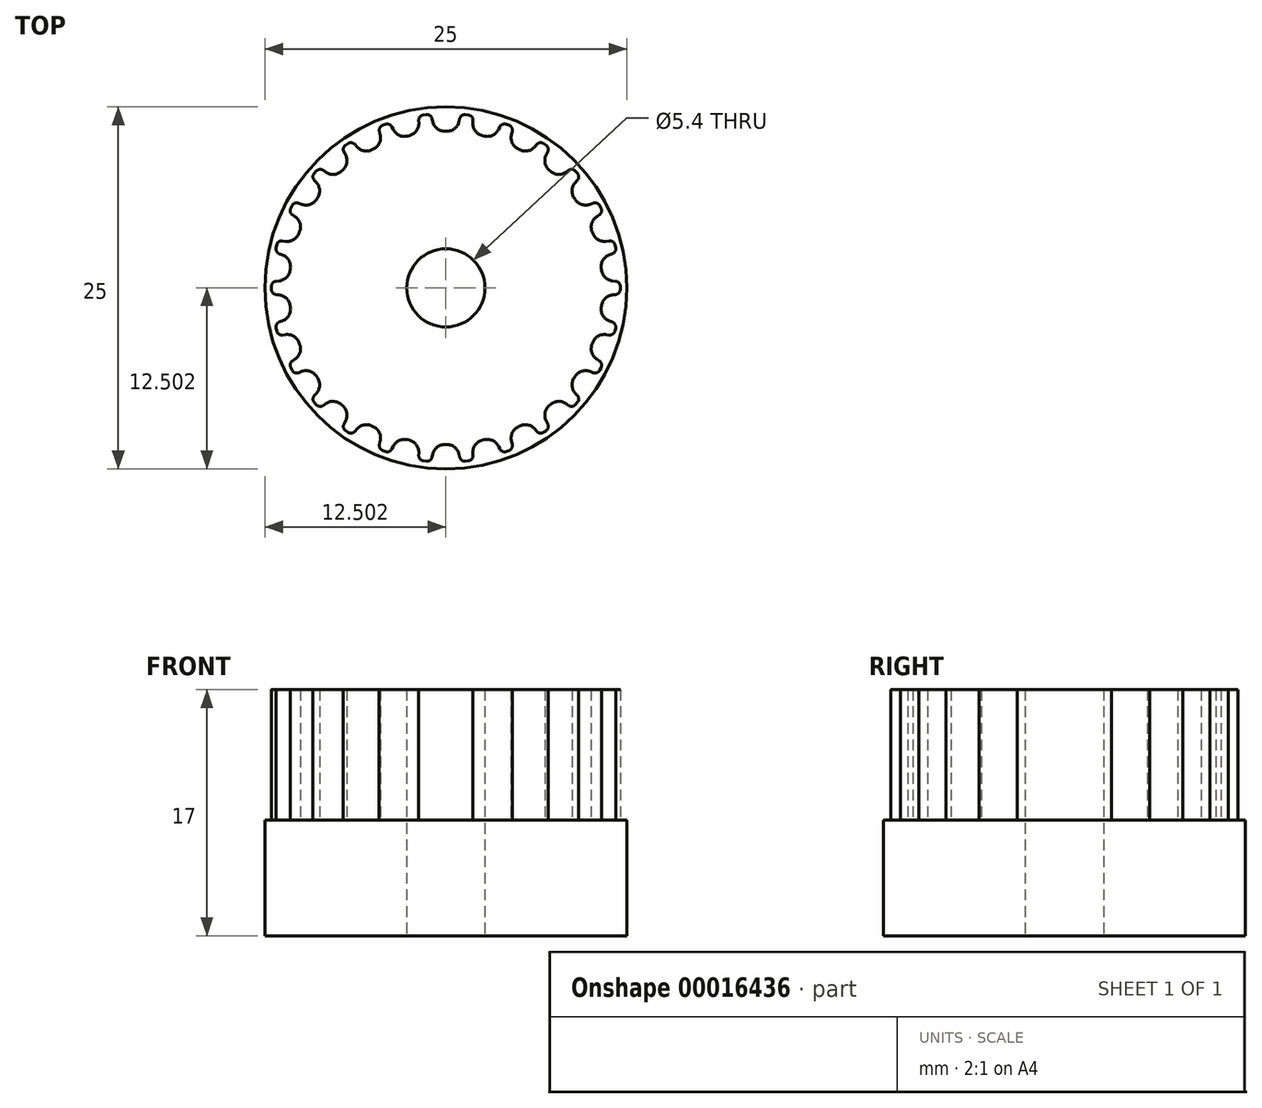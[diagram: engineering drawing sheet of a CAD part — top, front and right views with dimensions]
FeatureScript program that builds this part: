
annotation { "Feature Type Name" : "Feature", "Feature Type Description" : "" }
export const myFeature = defineFeature(function(context is Context, id is Id, definition is map)
    precondition{}
    {
        {
            var Q0;
            Q0=qCreatedBy(makeId("Top.planeOp"),FACE);
            var sketch = newSketch(context, id + "F0", { "sketchPlane" : qUnion([Q0])});
            skArc(sketch, "E0.20.0", {"start": v(-11.7, 0.46) * mm, "mid": v(-11.94, 0.35) * mm, "end": v(-12.03, 0.1) * mm});
            skArc(sketch, "E0.20.1", {"start": v(-10.73, -1.24) * mm, "mid": v(-11, -0.72) * mm, "end": v(-11.51, -0.48) * mm});
            skArc(sketch, "E0.20.2", {"start": v(-12.03, -0.1) * mm, "mid": v(-11.94, -0.34) * mm, "end": v(-11.7, -0.46) * mm});
            skArc(sketch, "E0.20.3", {"start": v(-11.51, 0.48) * mm, "mid": v(-11, 0.73) * mm, "end": v(-10.73, 1.24) * mm});
            skLineSegment(sketch, "E0.20.5", {"start": v(-10.72, -1.37) * mm, "end": v(-10.73, -1.24) * mm});
            skLineSegment(sketch, "E1", {"start": v(-11.51, 0.48) * mm, "end": v(-11.7, 0.46) * mm});
            skLineSegment(sketch, "E2", {"start": v(-12.03, 0.1) * mm, "end": v(-12.03, -0.1) * mm});
            skLineSegment(sketch, "E3", {"start": v(-11.51, -0.48) * mm, "end": v(-11.7, -0.46) * mm});
            skArc(sketch, "E4.1.0", {"start": v(-11.48, -2.36) * mm, "mid": v(-11.68, -2.52) * mm, "end": v(-11.7, -2.78) * mm});
            skArc(sketch, "E4.1.1", {"start": v(-11.66, -2.98) * mm, "mid": v(-11.51, -3.2) * mm, "end": v(-11.26, -3.25) * mm});
            skArc(sketch, "E4.1.2", {"start": v(-11.3, -2.3) * mm, "mid": v(-10.84, -1.93) * mm, "end": v(-10.72, -1.37) * mm});
            skArc(sketch, "E4.1.3", {"start": v(-10.13, -3.77) * mm, "mid": v(-10.5, -3.33) * mm, "end": v(-11.06, -3.22) * mm});
            skLineSegment(sketch, "E4.1.4", {"start": v(-11.06, -3.22) * mm, "end": v(-11.26, -3.25) * mm});
            skLineSegment(sketch, "E4.1.5", {"start": v(-11.7, -2.78) * mm, "end": v(-11.66, -2.98) * mm});
            skLineSegment(sketch, "E4.1.6", {"start": v(-11.3, -2.3) * mm, "end": v(-11.48, -2.36) * mm});
            skLineSegment(sketch, "E4.1.7", {"start": v(-10.08, -3.9) * mm, "end": v(-10.13, -3.77) * mm});
            skArc(sketch, "E4.2.0", {"start": v(-10.58, -5.04) * mm, "mid": v(-10.73, -5.25) * mm, "end": v(-10.7, -5.5) * mm});
            skArc(sketch, "E4.2.1", {"start": v(-10.6, -5.69) * mm, "mid": v(-10.41, -5.86) * mm, "end": v(-10.15, -5.85) * mm});
            skArc(sketch, "E4.2.2", {"start": v(-10.42, -4.93) * mm, "mid": v(-10.07, -4.47) * mm, "end": v(-10.08, -3.9) * mm});
            skArc(sketch, "E4.2.3", {"start": v(-8.93, -6.1) * mm, "mid": v(-9.4, -5.75) * mm, "end": v(-9.97, -5.78) * mm});
            skLineSegment(sketch, "E4.2.4", {"start": v(-9.97, -5.78) * mm, "end": v(-10.15, -5.85) * mm});
            skLineSegment(sketch, "E4.2.5", {"start": v(-10.7, -5.5) * mm, "end": v(-10.6, -5.69) * mm});
            skLineSegment(sketch, "E4.2.6", {"start": v(-10.42, -4.93) * mm, "end": v(-10.58, -5.04) * mm});
            skLineSegment(sketch, "E4.2.7", {"start": v(-8.85, -6.2) * mm, "end": v(-8.93, -6.1) * mm});
            skArc(sketch, "E4.3.0", {"start": v(-9.07, -7.43) * mm, "mid": v(-9.16, -7.67) * mm, "end": v(-9.07, -7.9) * mm});
            skArc(sketch, "E4.3.1", {"start": v(-8.94, -8.06) * mm, "mid": v(-8.7, -8.18) * mm, "end": v(-8.46, -8.12) * mm});
            skArc(sketch, "E4.3.2", {"start": v(-8.93, -7.28) * mm, "mid": v(-8.7, -6.75) * mm, "end": v(-8.85, -6.2) * mm});
            skArc(sketch, "E4.3.3", {"start": v(-7.2, -8.05) * mm, "mid": v(-7.74, -7.84) * mm, "end": v(-8.3, -8) * mm});
            skLineSegment(sketch, "E4.3.4", {"start": v(-8.3, -8) * mm, "end": v(-8.46, -8.12) * mm});
            skLineSegment(sketch, "E4.3.5", {"start": v(-9.07, -7.9) * mm, "end": v(-8.94, -8.06) * mm});
            skLineSegment(sketch, "E4.3.6", {"start": v(-8.93, -7.28) * mm, "end": v(-9.07, -7.43) * mm});
            skLineSegment(sketch, "E4.3.7", {"start": v(-7.11, -8.14) * mm, "end": v(-7.2, -8.05) * mm});
            skArc(sketch, "E4.4.0", {"start": v(-7.03, -9.38) * mm, "mid": v(-7.06, -9.64) * mm, "end": v(-6.92, -9.85) * mm});
            skArc(sketch, "E4.4.1", {"start": v(-6.75, -9.97) * mm, "mid": v(-6.5, -10.03) * mm, "end": v(-6.27, -9.9) * mm});
            skArc(sketch, "E4.4.2", {"start": v(-6.93, -9.21) * mm, "mid": v(-6.83, -8.64) * mm, "end": v(-7.11, -8.14) * mm});
            skArc(sketch, "E4.4.3", {"start": v(-5.07, -9.55) * mm, "mid": v(-5.64, -9.46) * mm, "end": v(-6.14, -9.76) * mm});
            skLineSegment(sketch, "E4.4.4", {"start": v(-6.14, -9.76) * mm, "end": v(-6.27, -9.9) * mm});
            skLineSegment(sketch, "E4.4.5", {"start": v(-6.92, -9.85) * mm, "end": v(-6.75, -9.97) * mm});
            skLineSegment(sketch, "E4.4.6", {"start": v(-6.93, -9.21) * mm, "end": v(-7.03, -9.38) * mm});
            skLineSegment(sketch, "E4.4.7", {"start": v(-4.96, -9.6) * mm, "end": v(-5.07, -9.55) * mm});
            skArc(sketch, "E4.5.0", {"start": v(-4.57, -10.8) * mm, "mid": v(-4.55, -11.05) * mm, "end": v(-4.36, -11.22) * mm});
            skArc(sketch, "E4.5.1", {"start": v(-4.16, -11.3) * mm, "mid": v(-3.9, -11.3) * mm, "end": v(-3.71, -11.12) * mm});
            skArc(sketch, "E4.5.2", {"start": v(-4.52, -10.6) * mm, "mid": v(-4.57, -10.03) * mm, "end": v(-4.96, -9.6) * mm});
            skArc(sketch, "E4.5.3", {"start": v(-2.64, -10.49) * mm, "mid": v(-3.21, -10.54) * mm, "end": v(-3.63, -10.94) * mm});
            skLineSegment(sketch, "E4.5.4", {"start": v(-3.63, -10.94) * mm, "end": v(-3.71, -11.12) * mm});
            skLineSegment(sketch, "E4.5.5", {"start": v(-4.36, -11.22) * mm, "end": v(-4.16, -11.3) * mm});
            skLineSegment(sketch, "E4.5.6", {"start": v(-4.52, -10.6) * mm, "end": v(-4.57, -10.8) * mm});
            skLineSegment(sketch, "E4.5.7", {"start": v(-2.51, -10.52) * mm, "end": v(-2.64, -10.49) * mm});
            skArc(sketch, "E4.6.0", {"start": v(-1.86, -11.58) * mm, "mid": v(-1.77, -11.82) * mm, "end": v(-1.54, -11.94) * mm});
            skArc(sketch, "E4.6.1", {"start": v(-1.34, -11.97) * mm, "mid": v(-1.09, -11.9) * mm, "end": v(-0.94, -11.69) * mm});
            skArc(sketch, "E4.6.2", {"start": v(-1.85, -11.38) * mm, "mid": v(-2.03, -10.83) * mm, "end": v(-2.51, -10.52) * mm});
            skArc(sketch, "E4.6.3", {"start": v(-0.05, -10.82) * mm, "mid": v(-0.6, -11) * mm, "end": v(-0.9, -11.5) * mm});
            skLineSegment(sketch, "E4.6.4", {"start": v(-0.9, -11.5) * mm, "end": v(-0.94, -11.69) * mm});
            skLineSegment(sketch, "E4.6.5", {"start": v(-1.54, -11.94) * mm, "end": v(-1.34, -11.97) * mm});
            skLineSegment(sketch, "E4.6.6", {"start": v(-1.85, -11.38) * mm, "end": v(-1.86, -11.58) * mm});
            skLineSegment(sketch, "E4.6.7", {"start": v(0.08, -10.82) * mm, "end": v(-0.05, -10.82) * mm});
            skArc(sketch, "E4.7.0", {"start": v(0.97, -11.69) * mm, "mid": v(1.11, -11.9) * mm, "end": v(1.36, -11.97) * mm});
            skArc(sketch, "E4.7.1", {"start": v(1.57, -11.94) * mm, "mid": v(1.8, -11.82) * mm, "end": v(1.88, -11.58) * mm});
            skArc(sketch, "E4.7.2", {"start": v(0.93, -11.5) * mm, "mid": v(0.62, -11) * mm, "end": v(0.08, -10.82) * mm});
            skArc(sketch, "E4.7.3", {"start": v(2.54, -10.52) * mm, "mid": v(2.06, -10.83) * mm, "end": v(1.88, -11.38) * mm});
            skLineSegment(sketch, "E4.7.4", {"start": v(1.88, -11.38) * mm, "end": v(1.88, -11.58) * mm});
            skLineSegment(sketch, "E4.7.5", {"start": v(1.36, -11.97) * mm, "end": v(1.57, -11.94) * mm});
            skLineSegment(sketch, "E4.7.6", {"start": v(0.93, -11.5) * mm, "end": v(0.97, -11.69) * mm});
            skLineSegment(sketch, "E4.7.7", {"start": v(2.66, -10.49) * mm, "end": v(2.54, -10.52) * mm});
            skArc(sketch, "E4.8.0", {"start": v(3.74, -11.12) * mm, "mid": v(3.93, -11.3) * mm, "end": v(4.19, -11.3) * mm});
            skArc(sketch, "E4.8.1", {"start": v(4.38, -11.23) * mm, "mid": v(4.57, -11.05) * mm, "end": v(4.6, -10.8) * mm});
            skArc(sketch, "E4.8.2", {"start": v(3.65, -10.94) * mm, "mid": v(3.24, -10.54) * mm, "end": v(2.66, -10.49) * mm});
            skArc(sketch, "E4.8.3", {"start": v(4.98, -9.6) * mm, "mid": v(4.6, -10.03) * mm, "end": v(4.55, -10.6) * mm});
            skLineSegment(sketch, "E4.8.4", {"start": v(4.55, -10.6) * mm, "end": v(4.6, -10.8) * mm});
            skLineSegment(sketch, "E4.8.5", {"start": v(4.19, -11.3) * mm, "end": v(4.38, -11.23) * mm});
            skLineSegment(sketch, "E4.8.6", {"start": v(3.65, -10.94) * mm, "end": v(3.74, -11.12) * mm});
            skLineSegment(sketch, "E4.8.7", {"start": v(5.1, -9.55) * mm, "end": v(4.98, -9.6) * mm});
            skArc(sketch, "E4.9.0", {"start": v(6.3, -9.9) * mm, "mid": v(6.52, -10.03) * mm, "end": v(6.77, -9.97) * mm});
            skArc(sketch, "E4.9.1", {"start": v(6.94, -9.85) * mm, "mid": v(7.09, -9.64) * mm, "end": v(7.05, -9.38) * mm});
            skArc(sketch, "E4.9.2", {"start": v(6.17, -9.76) * mm, "mid": v(5.67, -9.46) * mm, "end": v(5.1, -9.55) * mm});
            skArc(sketch, "E4.9.3", {"start": v(7.14, -8.14) * mm, "mid": v(6.86, -8.64) * mm, "end": v(6.95, -9.21) * mm});
            skLineSegment(sketch, "E4.9.4", {"start": v(6.95, -9.21) * mm, "end": v(7.05, -9.38) * mm});
            skLineSegment(sketch, "E4.9.5", {"start": v(6.77, -9.97) * mm, "end": v(6.94, -9.85) * mm});
            skLineSegment(sketch, "E4.9.6", {"start": v(6.17, -9.76) * mm, "end": v(6.3, -9.9) * mm});
            skLineSegment(sketch, "E4.9.7", {"start": v(7.23, -8.05) * mm, "end": v(7.14, -8.14) * mm});
            skArc(sketch, "E4.10.0", {"start": v(8.48, -8.12) * mm, "mid": v(8.73, -8.18) * mm, "end": v(8.96, -8.07) * mm});
            skArc(sketch, "E4.10.1", {"start": v(9.1, -7.91) * mm, "mid": v(9.19, -7.67) * mm, "end": v(9.1, -7.43) * mm});
            skArc(sketch, "E4.10.2", {"start": v(8.32, -8) * mm, "mid": v(7.77, -7.84) * mm, "end": v(7.23, -8.05) * mm});
            skArc(sketch, "E4.10.3", {"start": v(8.88, -6.2) * mm, "mid": v(8.73, -6.75) * mm, "end": v(8.96, -7.28) * mm});
            skLineSegment(sketch, "E4.10.4", {"start": v(8.96, -7.28) * mm, "end": v(9.1, -7.43) * mm});
            skLineSegment(sketch, "E4.10.5", {"start": v(8.96, -8.07) * mm, "end": v(9.1, -7.91) * mm});
            skLineSegment(sketch, "E4.10.6", {"start": v(8.32, -8) * mm, "end": v(8.48, -8.12) * mm});
            skLineSegment(sketch, "E4.10.7", {"start": v(8.95, -6.1) * mm, "end": v(8.88, -6.2) * mm});
            skArc(sketch, "E4.11.0", {"start": v(10.18, -5.85) * mm, "mid": v(10.44, -5.86) * mm, "end": v(10.63, -5.69) * mm});
            skArc(sketch, "E4.11.1", {"start": v(10.73, -5.5) * mm, "mid": v(10.76, -5.25) * mm, "end": v(10.6, -5.04) * mm});
            skArc(sketch, "E4.11.2", {"start": v(10, -5.78) * mm, "mid": v(9.42, -5.75) * mm, "end": v(8.95, -6.1) * mm});
            skArc(sketch, "E4.11.3", {"start": v(10.1, -3.9) * mm, "mid": v(10.1, -4.47) * mm, "end": v(10.44, -4.93) * mm});
            skLineSegment(sketch, "E4.11.4", {"start": v(10.44, -4.93) * mm, "end": v(10.6, -5.04) * mm});
            skLineSegment(sketch, "E4.11.5", {"start": v(10.63, -5.69) * mm, "end": v(10.73, -5.5) * mm});
            skLineSegment(sketch, "E4.11.6", {"start": v(10, -5.78) * mm, "end": v(10.18, -5.85) * mm});
            skLineSegment(sketch, "E4.11.7", {"start": v(10.15, -3.77) * mm, "end": v(10.1, -3.9) * mm});
            skArc(sketch, "E4.12.0", {"start": v(11.28, -3.25) * mm, "mid": v(11.54, -3.2) * mm, "end": v(11.68, -2.98) * mm});
            skArc(sketch, "E4.12.1", {"start": v(11.73, -2.78) * mm, "mid": v(11.7, -2.52) * mm, "end": v(11.5, -2.36) * mm});
            skArc(sketch, "E4.12.2", {"start": v(11.09, -3.22) * mm, "mid": v(10.52, -3.33) * mm, "end": v(10.15, -3.77) * mm});
            skArc(sketch, "E4.12.3", {"start": v(10.74, -1.37) * mm, "mid": v(10.87, -1.93) * mm, "end": v(11.32, -2.3) * mm});
            skLineSegment(sketch, "E4.12.4", {"start": v(11.32, -2.3) * mm, "end": v(11.5, -2.36) * mm});
            skLineSegment(sketch, "E4.12.5", {"start": v(11.68, -2.98) * mm, "end": v(11.73, -2.78) * mm});
            skLineSegment(sketch, "E4.12.6", {"start": v(11.09, -3.22) * mm, "end": v(11.28, -3.25) * mm});
            skLineSegment(sketch, "E4.12.7", {"start": v(10.76, -1.24) * mm, "end": v(10.74, -1.37) * mm});
            skArc(sketch, "E4.13.0", {"start": v(11.73, -0.46) * mm, "mid": v(11.96, -0.34) * mm, "end": v(12.06, -0.1) * mm});
            skArc(sketch, "E4.13.1", {"start": v(12.06, 0.1) * mm, "mid": v(11.97, 0.35) * mm, "end": v(11.73, 0.46) * mm});
            skArc(sketch, "E4.13.2", {"start": v(11.54, -0.48) * mm, "mid": v(11.01, -0.72) * mm, "end": v(10.76, -1.24) * mm});
            skArc(sketch, "E4.13.3", {"start": v(10.76, 1.24) * mm, "mid": v(11.01, 0.73) * mm, "end": v(11.54, 0.48) * mm});
            skLineSegment(sketch, "E4.13.4", {"start": v(11.54, 0.48) * mm, "end": v(11.73, 0.46) * mm});
            skLineSegment(sketch, "E4.13.5", {"start": v(12.06, -0.1) * mm, "end": v(12.06, 0.1) * mm});
            skLineSegment(sketch, "E4.13.6", {"start": v(11.54, -0.48) * mm, "end": v(11.73, -0.46) * mm});
            skLineSegment(sketch, "E4.13.7", {"start": v(10.74, 1.37) * mm, "end": v(10.76, 1.24) * mm});
            skArc(sketch, "E4.14.0", {"start": v(11.5, 2.36) * mm, "mid": v(11.7, 2.53) * mm, "end": v(11.73, 2.78) * mm});
            skArc(sketch, "E4.14.1", {"start": v(11.68, 2.98) * mm, "mid": v(11.54, 3.2) * mm, "end": v(11.28, 3.25) * mm});
            skArc(sketch, "E4.14.2", {"start": v(11.32, 2.3) * mm, "mid": v(10.87, 1.93) * mm, "end": v(10.74, 1.37) * mm});
            skArc(sketch, "E4.14.3", {"start": v(10.15, 3.78) * mm, "mid": v(10.52, 3.34) * mm, "end": v(11.09, 3.23) * mm});
            skLineSegment(sketch, "E4.14.4", {"start": v(11.09, 3.23) * mm, "end": v(11.28, 3.25) * mm});
            skLineSegment(sketch, "E4.14.5", {"start": v(11.73, 2.78) * mm, "end": v(11.68, 2.98) * mm});
            skLineSegment(sketch, "E4.14.6", {"start": v(11.32, 2.3) * mm, "end": v(11.5, 2.36) * mm});
            skLineSegment(sketch, "E4.14.7", {"start": v(10.1, 3.9) * mm, "end": v(10.15, 3.78) * mm});
            skArc(sketch, "E4.15.0", {"start": v(10.6, 5.04) * mm, "mid": v(10.76, 5.25) * mm, "end": v(10.73, 5.5) * mm});
            skArc(sketch, "E4.15.1", {"start": v(10.63, 5.7) * mm, "mid": v(10.44, 5.86) * mm, "end": v(10.18, 5.86) * mm});
            skArc(sketch, "E4.15.2", {"start": v(10.44, 4.93) * mm, "mid": v(10.1, 4.48) * mm, "end": v(10.1, 3.9) * mm});
            skArc(sketch, "E4.15.3", {"start": v(8.95, 6.1) * mm, "mid": v(9.42, 5.76) * mm, "end": v(10, 5.78) * mm});
            skLineSegment(sketch, "E4.15.4", {"start": v(10, 5.78) * mm, "end": v(10.18, 5.86) * mm});
            skLineSegment(sketch, "E4.15.5", {"start": v(10.73, 5.5) * mm, "end": v(10.63, 5.7) * mm});
            skLineSegment(sketch, "E4.15.6", {"start": v(10.44, 4.93) * mm, "end": v(10.6, 5.04) * mm});
            skLineSegment(sketch, "E4.15.7", {"start": v(8.88, 6.2) * mm, "end": v(8.95, 6.1) * mm});
            skArc(sketch, "E4.16.0", {"start": v(9.1, 7.43) * mm, "mid": v(9.19, 7.67) * mm, "end": v(9.1, 7.91) * mm});
            skArc(sketch, "E4.16.1", {"start": v(8.96, 8.07) * mm, "mid": v(8.73, 8.19) * mm, "end": v(8.48, 8.12) * mm});
            skArc(sketch, "E4.16.2", {"start": v(8.96, 7.29) * mm, "mid": v(8.73, 6.76) * mm, "end": v(8.88, 6.2) * mm});
            skArc(sketch, "E4.16.3", {"start": v(7.23, 8.06) * mm, "mid": v(7.77, 7.84) * mm, "end": v(8.32, 8) * mm});
            skLineSegment(sketch, "E4.16.4", {"start": v(8.32, 8) * mm, "end": v(8.48, 8.12) * mm});
            skLineSegment(sketch, "E4.16.5", {"start": v(9.1, 7.91) * mm, "end": v(8.96, 8.07) * mm});
            skLineSegment(sketch, "E4.16.6", {"start": v(8.96, 7.29) * mm, "end": v(9.1, 7.43) * mm});
            skLineSegment(sketch, "E4.16.7", {"start": v(7.14, 8.14) * mm, "end": v(7.23, 8.06) * mm});
            skArc(sketch, "E4.17.0", {"start": v(7.05, 9.39) * mm, "mid": v(7.09, 9.64) * mm, "end": v(6.94, 9.86) * mm});
            skArc(sketch, "E4.17.1", {"start": v(6.77, 9.97) * mm, "mid": v(6.52, 10.04) * mm, "end": v(6.3, 9.91) * mm});
            skArc(sketch, "E4.17.2", {"start": v(6.95, 9.22) * mm, "mid": v(6.86, 8.65) * mm, "end": v(7.14, 8.14) * mm});
            skArc(sketch, "E4.17.3", {"start": v(5.1, 9.55) * mm, "mid": v(5.67, 9.47) * mm, "end": v(6.16, 9.76) * mm});
            skLineSegment(sketch, "E4.17.4", {"start": v(6.16, 9.76) * mm, "end": v(6.3, 9.91) * mm});
            skLineSegment(sketch, "E4.17.5", {"start": v(6.94, 9.86) * mm, "end": v(6.77, 9.97) * mm});
            skLineSegment(sketch, "E4.17.6", {"start": v(6.95, 9.22) * mm, "end": v(7.05, 9.39) * mm});
            skLineSegment(sketch, "E4.17.7", {"start": v(4.98, 9.61) * mm, "end": v(5.1, 9.55) * mm});
            skArc(sketch, "E4.18.0", {"start": v(4.6, 10.8) * mm, "mid": v(4.57, 11.06) * mm, "end": v(4.38, 11.23) * mm});
            skArc(sketch, "E4.18.1", {"start": v(4.19, 11.3) * mm, "mid": v(3.93, 11.3) * mm, "end": v(3.74, 11.13) * mm});
            skArc(sketch, "E4.18.2", {"start": v(4.55, 10.6) * mm, "mid": v(4.59, 10.03) * mm, "end": v(4.98, 9.61) * mm});
            skArc(sketch, "E4.18.3", {"start": v(2.66, 10.5) * mm, "mid": v(3.24, 10.55) * mm, "end": v(3.65, 10.95) * mm});
            skLineSegment(sketch, "E4.18.4", {"start": v(3.65, 10.95) * mm, "end": v(3.74, 11.13) * mm});
            skLineSegment(sketch, "E4.18.5", {"start": v(4.38, 11.23) * mm, "end": v(4.19, 11.3) * mm});
            skLineSegment(sketch, "E4.18.6", {"start": v(4.55, 10.6) * mm, "end": v(4.6, 10.8) * mm});
            skLineSegment(sketch, "E4.18.7", {"start": v(2.54, 10.52) * mm, "end": v(2.66, 10.5) * mm});
            skArc(sketch, "E4.19.0", {"start": v(1.88, 11.58) * mm, "mid": v(1.8, 11.83) * mm, "end": v(1.57, 11.95) * mm});
            skArc(sketch, "E4.19.1", {"start": v(1.36, 11.97) * mm, "mid": v(1.11, 11.91) * mm, "end": v(0.97, 11.7) * mm});
            skArc(sketch, "E4.19.2", {"start": v(1.88, 11.39) * mm, "mid": v(2.06, 10.84) * mm, "end": v(2.54, 10.52) * mm});
            skArc(sketch, "E4.19.3", {"start": v(0.08, 10.82) * mm, "mid": v(0.62, 11.01) * mm, "end": v(0.93, 11.5) * mm});
            skLineSegment(sketch, "E4.19.4", {"start": v(0.93, 11.5) * mm, "end": v(0.97, 11.7) * mm});
            skLineSegment(sketch, "E4.19.5", {"start": v(1.57, 11.95) * mm, "end": v(1.36, 11.97) * mm});
            skLineSegment(sketch, "E4.19.6", {"start": v(1.88, 11.39) * mm, "end": v(1.88, 11.58) * mm});
            skLineSegment(sketch, "E4.19.7", {"start": v(-0.05, 10.82) * mm, "end": v(0.08, 10.82) * mm});
            skArc(sketch, "E4.20.0", {"start": v(-0.94, 11.7) * mm, "mid": v(-1.09, 11.9) * mm, "end": v(-1.34, 11.97) * mm});
            skArc(sketch, "E4.20.1", {"start": v(-1.54, 11.95) * mm, "mid": v(-1.77, 11.83) * mm, "end": v(-1.86, 11.58) * mm});
            skArc(sketch, "E4.20.2", {"start": v(-0.9, 11.5) * mm, "mid": v(-0.6, 11.01) * mm, "end": v(-0.05, 10.82) * mm});
            skArc(sketch, "E4.20.3", {"start": v(-2.51, 10.52) * mm, "mid": v(-2.03, 10.84) * mm, "end": v(-1.85, 11.39) * mm});
            skLineSegment(sketch, "E4.20.4", {"start": v(-1.85, 11.39) * mm, "end": v(-1.86, 11.58) * mm});
            skLineSegment(sketch, "E4.20.5", {"start": v(-1.34, 11.97) * mm, "end": v(-1.54, 11.95) * mm});
            skLineSegment(sketch, "E4.20.6", {"start": v(-0.9, 11.5) * mm, "end": v(-0.94, 11.7) * mm});
            skLineSegment(sketch, "E4.20.7", {"start": v(-2.64, 10.5) * mm, "end": v(-2.51, 10.52) * mm});
            skArc(sketch, "E4.21.0", {"start": v(-3.71, 11.13) * mm, "mid": v(-3.9, 11.3) * mm, "end": v(-4.16, 11.3) * mm});
            skArc(sketch, "E4.21.1", {"start": v(-4.35, 11.23) * mm, "mid": v(-4.55, 11.06) * mm, "end": v(-4.57, 10.8) * mm});
            skArc(sketch, "E4.21.2", {"start": v(-3.63, 10.95) * mm, "mid": v(-3.21, 10.55) * mm, "end": v(-2.64, 10.5) * mm});
            skArc(sketch, "E4.21.3", {"start": v(-4.96, 9.61) * mm, "mid": v(-4.57, 10.03) * mm, "end": v(-4.52, 10.6) * mm});
            skLineSegment(sketch, "E4.21.4", {"start": v(-4.52, 10.6) * mm, "end": v(-4.57, 10.8) * mm});
            skLineSegment(sketch, "E4.21.5", {"start": v(-4.16, 11.3) * mm, "end": v(-4.35, 11.23) * mm});
            skLineSegment(sketch, "E4.21.6", {"start": v(-3.63, 10.95) * mm, "end": v(-3.71, 11.13) * mm});
            skLineSegment(sketch, "E4.21.7", {"start": v(-5.07, 9.55) * mm, "end": v(-4.96, 9.61) * mm});
            skArc(sketch, "E4.22.0", {"start": v(-6.27, 9.91) * mm, "mid": v(-6.5, 10.03) * mm, "end": v(-6.74, 9.98) * mm});
            skArc(sketch, "E4.22.1", {"start": v(-6.91, 9.86) * mm, "mid": v(-7.06, 9.64) * mm, "end": v(-7.03, 9.39) * mm});
            skArc(sketch, "E4.22.2", {"start": v(-6.14, 9.76) * mm, "mid": v(-5.64, 9.47) * mm, "end": v(-5.07, 9.55) * mm});
            skArc(sketch, "E4.22.3", {"start": v(-7.11, 8.14) * mm, "mid": v(-6.83, 8.65) * mm, "end": v(-6.93, 9.22) * mm});
            skLineSegment(sketch, "E4.22.4", {"start": v(-6.93, 9.22) * mm, "end": v(-7.03, 9.39) * mm});
            skLineSegment(sketch, "E4.22.5", {"start": v(-6.74, 9.98) * mm, "end": v(-6.91, 9.86) * mm});
            skLineSegment(sketch, "E4.22.6", {"start": v(-6.14, 9.76) * mm, "end": v(-6.27, 9.91) * mm});
            skLineSegment(sketch, "E4.22.7", {"start": v(-7.2, 8.06) * mm, "end": v(-7.11, 8.14) * mm});
            skArc(sketch, "E4.23.0", {"start": v(-8.46, 8.12) * mm, "mid": v(-8.7, 8.19) * mm, "end": v(-8.94, 8.07) * mm});
            skArc(sketch, "E4.23.1", {"start": v(-9.07, 7.91) * mm, "mid": v(-9.16, 7.67) * mm, "end": v(-9.07, 7.43) * mm});
            skArc(sketch, "E4.23.2", {"start": v(-8.3, 8) * mm, "mid": v(-7.74, 7.84) * mm, "end": v(-7.2, 8.06) * mm});
            skArc(sketch, "E4.23.3", {"start": v(-8.85, 6.2) * mm, "mid": v(-8.7, 6.76) * mm, "end": v(-8.93, 7.29) * mm});
            skLineSegment(sketch, "E4.23.4", {"start": v(-8.93, 7.29) * mm, "end": v(-9.07, 7.43) * mm});
            skLineSegment(sketch, "E4.23.5", {"start": v(-8.94, 8.07) * mm, "end": v(-9.07, 7.91) * mm});
            skLineSegment(sketch, "E4.23.6", {"start": v(-8.3, 8) * mm, "end": v(-8.46, 8.12) * mm});
            skLineSegment(sketch, "E4.23.7", {"start": v(-8.93, 6.1) * mm, "end": v(-8.85, 6.2) * mm});
            skArc(sketch, "E4.24.0", {"start": v(-10.15, 5.86) * mm, "mid": v(-10.41, 5.86) * mm, "end": v(-10.6, 5.7) * mm});
            skArc(sketch, "E4.24.1", {"start": v(-10.7, 5.51) * mm, "mid": v(-10.73, 5.25) * mm, "end": v(-10.58, 5.04) * mm});
            skArc(sketch, "E4.24.2", {"start": v(-9.97, 5.78) * mm, "mid": v(-9.4, 5.76) * mm, "end": v(-8.93, 6.1) * mm});
            skArc(sketch, "E4.24.3", {"start": v(-10.08, 3.9) * mm, "mid": v(-10.07, 4.47) * mm, "end": v(-10.42, 4.93) * mm});
            skLineSegment(sketch, "E4.24.4", {"start": v(-10.42, 4.93) * mm, "end": v(-10.58, 5.04) * mm});
            skLineSegment(sketch, "E4.24.5", {"start": v(-10.6, 5.7) * mm, "end": v(-10.7, 5.51) * mm});
            skLineSegment(sketch, "E4.24.6", {"start": v(-9.97, 5.78) * mm, "end": v(-10.15, 5.86) * mm});
            skLineSegment(sketch, "E4.24.7", {"start": v(-10.13, 3.78) * mm, "end": v(-10.08, 3.9) * mm});
            skArc(sketch, "E4.25.0", {"start": v(-11.26, 3.25) * mm, "mid": v(-11.51, 3.2) * mm, "end": v(-11.66, 2.99) * mm});
            skArc(sketch, "E4.25.1", {"start": v(-11.7, 2.79) * mm, "mid": v(-11.68, 2.53) * mm, "end": v(-11.48, 2.36) * mm});
            skArc(sketch, "E4.25.2", {"start": v(-11.06, 3.23) * mm, "mid": v(-10.5, 3.34) * mm, "end": v(-10.13, 3.78) * mm});
            skArc(sketch, "E4.25.3", {"start": v(-10.72, 1.37) * mm, "mid": v(-10.84, 1.93) * mm, "end": v(-11.3, 2.3) * mm});
            skLineSegment(sketch, "E4.25.4", {"start": v(-11.3, 2.3) * mm, "end": v(-11.48, 2.36) * mm});
            skLineSegment(sketch, "E4.25.5", {"start": v(-11.66, 2.99) * mm, "end": v(-11.7, 2.79) * mm});
            skLineSegment(sketch, "E4.25.6", {"start": v(-11.06, 3.23) * mm, "end": v(-11.26, 3.25) * mm});
            skLineSegment(sketch, "E4.25.7", {"start": v(-10.73, 1.24) * mm, "end": v(-10.72, 1.37) * mm});
            skPoint(sketch, "E4.center", {"position": v(0.01, 0) * mm});
            skCircle(sketch, "E5", {"center": v(0.01, 0) * mm, "radius": 2.7 * mm});
            skSolve(sketch);
        }
        {
            var Q0;
            Q0 = qSketchRegion(id + "F0", true);
            extrude(context, id + "F1", {"entities" : qUnion([Q0]), "depth" : 9 * mm});
        }
        {
            var Q0;
            Q0=makeQuery(id+"F1.opExtrude","CAP_FACE",FACE,{"disambiguationData":[OSD([sQuery(id+"F0.wireOp",EDGE,"E0.20.0"),sQuery(id+"F0.wireOp",EDGE,"E0.20.1"),sQuery(id+"F0.wireOp",EDGE,"E0.20.2"),sQuery(id+"F0.wireOp",EDGE,"E0.20.3"),sQuery(id+"F0.wireOp",EDGE,"E0.20.5"),sQuery(id+"F0.wireOp",EDGE,"E1"),sQuery(id+"F0.wireOp",EDGE,"E2"),sQuery(id+"F0.wireOp",EDGE,"E3"),sQuery(id+"F0.wireOp",EDGE,"E4.1.0"),sQuery(id+"F0.wireOp",EDGE,"E4.1.1"),sQuery(id+"F0.wireOp",EDGE,"E4.1.2"),sQuery(id+"F0.wireOp",EDGE,"E4.1.3"),sQuery(id+"F0.wireOp",EDGE,"E4.1.4"),sQuery(id+"F0.wireOp",EDGE,"E4.1.5"),sQuery(id+"F0.wireOp",EDGE,"E4.1.6"),sQuery(id+"F0.wireOp",EDGE,"E4.1.7"),sQuery(id+"F0.wireOp",EDGE,"E4.2.0"),sQuery(id+"F0.wireOp",EDGE,"E4.2.1"),sQuery(id+"F0.wireOp",EDGE,"E4.2.2"),sQuery(id+"F0.wireOp",EDGE,"E4.2.3"),sQuery(id+"F0.wireOp",EDGE,"E4.2.4"),sQuery(id+"F0.wireOp",EDGE,"E4.2.5"),sQuery(id+"F0.wireOp",EDGE,"E4.2.6"),sQuery(id+"F0.wireOp",EDGE,"E4.2.7"),sQuery(id+"F0.wireOp",EDGE,"E4.3.0"),sQuery(id+"F0.wireOp",EDGE,"E4.3.1"),sQuery(id+"F0.wireOp",EDGE,"E4.3.2"),sQuery(id+"F0.wireOp",EDGE,"E4.3.3"),sQuery(id+"F0.wireOp",EDGE,"E4.3.4"),sQuery(id+"F0.wireOp",EDGE,"E4.3.5"),sQuery(id+"F0.wireOp",EDGE,"E4.3.6"),sQuery(id+"F0.wireOp",EDGE,"E4.3.7"),sQuery(id+"F0.wireOp",EDGE,"E4.4.0"),sQuery(id+"F0.wireOp",EDGE,"E4.4.1"),sQuery(id+"F0.wireOp",EDGE,"E4.4.2"),sQuery(id+"F0.wireOp",EDGE,"E4.4.3"),sQuery(id+"F0.wireOp",EDGE,"E4.4.4"),sQuery(id+"F0.wireOp",EDGE,"E4.4.5"),sQuery(id+"F0.wireOp",EDGE,"E4.4.6"),sQuery(id+"F0.wireOp",EDGE,"E4.4.7"),sQuery(id+"F0.wireOp",EDGE,"E4.5.0"),sQuery(id+"F0.wireOp",EDGE,"E4.5.1"),sQuery(id+"F0.wireOp",EDGE,"E4.5.2"),sQuery(id+"F0.wireOp",EDGE,"E4.5.3"),sQuery(id+"F0.wireOp",EDGE,"E4.5.4"),sQuery(id+"F0.wireOp",EDGE,"E4.5.5"),sQuery(id+"F0.wireOp",EDGE,"E4.5.6"),sQuery(id+"F0.wireOp",EDGE,"E4.5.7"),sQuery(id+"F0.wireOp",EDGE,"E4.6.0"),sQuery(id+"F0.wireOp",EDGE,"E4.6.1"),sQuery(id+"F0.wireOp",EDGE,"E4.6.2"),sQuery(id+"F0.wireOp",EDGE,"E4.6.3"),sQuery(id+"F0.wireOp",EDGE,"E4.6.4"),sQuery(id+"F0.wireOp",EDGE,"E4.6.5"),sQuery(id+"F0.wireOp",EDGE,"E4.6.6"),sQuery(id+"F0.wireOp",EDGE,"E4.6.7"),sQuery(id+"F0.wireOp",EDGE,"E4.7.0"),sQuery(id+"F0.wireOp",EDGE,"E4.7.1"),sQuery(id+"F0.wireOp",EDGE,"E4.7.2"),sQuery(id+"F0.wireOp",EDGE,"E4.7.3"),sQuery(id+"F0.wireOp",EDGE,"E4.7.4"),sQuery(id+"F0.wireOp",EDGE,"E4.7.5"),sQuery(id+"F0.wireOp",EDGE,"E4.7.6"),sQuery(id+"F0.wireOp",EDGE,"E4.7.7"),sQuery(id+"F0.wireOp",EDGE,"E4.8.0"),sQuery(id+"F0.wireOp",EDGE,"E4.8.1"),sQuery(id+"F0.wireOp",EDGE,"E4.8.2"),sQuery(id+"F0.wireOp",EDGE,"E4.8.3"),sQuery(id+"F0.wireOp",EDGE,"E4.8.4"),sQuery(id+"F0.wireOp",EDGE,"E4.8.5"),sQuery(id+"F0.wireOp",EDGE,"E4.8.6"),sQuery(id+"F0.wireOp",EDGE,"E4.8.7"),sQuery(id+"F0.wireOp",EDGE,"E4.9.0"),sQuery(id+"F0.wireOp",EDGE,"E4.9.1"),sQuery(id+"F0.wireOp",EDGE,"E4.9.2"),sQuery(id+"F0.wireOp",EDGE,"E4.9.3"),sQuery(id+"F0.wireOp",EDGE,"E4.9.4"),sQuery(id+"F0.wireOp",EDGE,"E4.9.5"),sQuery(id+"F0.wireOp",EDGE,"E4.9.6"),sQuery(id+"F0.wireOp",EDGE,"E4.9.7"),sQuery(id+"F0.wireOp",EDGE,"E4.10.0"),sQuery(id+"F0.wireOp",EDGE,"E4.10.1"),sQuery(id+"F0.wireOp",EDGE,"E4.10.2"),sQuery(id+"F0.wireOp",EDGE,"E4.10.3"),sQuery(id+"F0.wireOp",EDGE,"E4.10.4"),sQuery(id+"F0.wireOp",EDGE,"E4.10.5"),sQuery(id+"F0.wireOp",EDGE,"E4.10.6"),sQuery(id+"F0.wireOp",EDGE,"E4.10.7"),sQuery(id+"F0.wireOp",EDGE,"E4.11.0"),sQuery(id+"F0.wireOp",EDGE,"E4.11.1"),sQuery(id+"F0.wireOp",EDGE,"E4.11.2"),sQuery(id+"F0.wireOp",EDGE,"E4.11.3"),sQuery(id+"F0.wireOp",EDGE,"E4.11.4"),sQuery(id+"F0.wireOp",EDGE,"E4.11.5"),sQuery(id+"F0.wireOp",EDGE,"E4.11.6"),sQuery(id+"F0.wireOp",EDGE,"E4.11.7"),sQuery(id+"F0.wireOp",EDGE,"E4.12.0"),sQuery(id+"F0.wireOp",EDGE,"E4.12.1"),sQuery(id+"F0.wireOp",EDGE,"E4.12.2"),sQuery(id+"F0.wireOp",EDGE,"E4.12.3"),sQuery(id+"F0.wireOp",EDGE,"E4.12.4"),sQuery(id+"F0.wireOp",EDGE,"E4.12.5"),sQuery(id+"F0.wireOp",EDGE,"E4.12.6"),sQuery(id+"F0.wireOp",EDGE,"E4.12.7"),sQuery(id+"F0.wireOp",EDGE,"E4.13.0"),sQuery(id+"F0.wireOp",EDGE,"E4.13.1"),sQuery(id+"F0.wireOp",EDGE,"E4.13.2"),sQuery(id+"F0.wireOp",EDGE,"E4.13.3"),sQuery(id+"F0.wireOp",EDGE,"E4.13.4"),sQuery(id+"F0.wireOp",EDGE,"E4.13.5"),sQuery(id+"F0.wireOp",EDGE,"E4.13.6"),sQuery(id+"F0.wireOp",EDGE,"E4.13.7"),sQuery(id+"F0.wireOp",EDGE,"E4.14.0"),sQuery(id+"F0.wireOp",EDGE,"E4.14.1"),sQuery(id+"F0.wireOp",EDGE,"E4.14.2"),sQuery(id+"F0.wireOp",EDGE,"E4.14.3"),sQuery(id+"F0.wireOp",EDGE,"E4.14.4"),sQuery(id+"F0.wireOp",EDGE,"E4.14.5"),sQuery(id+"F0.wireOp",EDGE,"E4.14.6"),sQuery(id+"F0.wireOp",EDGE,"E4.14.7"),sQuery(id+"F0.wireOp",EDGE,"E4.15.0"),sQuery(id+"F0.wireOp",EDGE,"E4.15.1"),sQuery(id+"F0.wireOp",EDGE,"E4.15.2"),sQuery(id+"F0.wireOp",EDGE,"E4.15.3"),sQuery(id+"F0.wireOp",EDGE,"E4.15.4"),sQuery(id+"F0.wireOp",EDGE,"E4.15.5"),sQuery(id+"F0.wireOp",EDGE,"E4.15.6"),sQuery(id+"F0.wireOp",EDGE,"E4.15.7"),sQuery(id+"F0.wireOp",EDGE,"E4.16.0"),sQuery(id+"F0.wireOp",EDGE,"E4.16.1"),sQuery(id+"F0.wireOp",EDGE,"E4.16.2"),sQuery(id+"F0.wireOp",EDGE,"E4.16.3"),sQuery(id+"F0.wireOp",EDGE,"E4.16.4"),sQuery(id+"F0.wireOp",EDGE,"E4.16.5"),sQuery(id+"F0.wireOp",EDGE,"E4.16.6"),sQuery(id+"F0.wireOp",EDGE,"E4.16.7"),sQuery(id+"F0.wireOp",EDGE,"E4.17.0"),sQuery(id+"F0.wireOp",EDGE,"E4.17.1"),sQuery(id+"F0.wireOp",EDGE,"E4.17.2"),sQuery(id+"F0.wireOp",EDGE,"E4.17.3"),sQuery(id+"F0.wireOp",EDGE,"E4.17.4"),sQuery(id+"F0.wireOp",EDGE,"E4.17.5"),sQuery(id+"F0.wireOp",EDGE,"E4.17.6"),sQuery(id+"F0.wireOp",EDGE,"E4.17.7"),sQuery(id+"F0.wireOp",EDGE,"E4.18.0"),sQuery(id+"F0.wireOp",EDGE,"E4.18.1"),sQuery(id+"F0.wireOp",EDGE,"E4.18.2"),sQuery(id+"F0.wireOp",EDGE,"E4.18.3"),sQuery(id+"F0.wireOp",EDGE,"E4.18.4"),sQuery(id+"F0.wireOp",EDGE,"E4.18.5"),sQuery(id+"F0.wireOp",EDGE,"E4.18.6"),sQuery(id+"F0.wireOp",EDGE,"E4.18.7"),sQuery(id+"F0.wireOp",EDGE,"E4.19.0"),sQuery(id+"F0.wireOp",EDGE,"E4.19.1"),sQuery(id+"F0.wireOp",EDGE,"E4.19.2"),sQuery(id+"F0.wireOp",EDGE,"E4.19.3"),sQuery(id+"F0.wireOp",EDGE,"E4.19.4"),sQuery(id+"F0.wireOp",EDGE,"E4.19.5"),sQuery(id+"F0.wireOp",EDGE,"E4.19.6"),sQuery(id+"F0.wireOp",EDGE,"E4.19.7"),sQuery(id+"F0.wireOp",EDGE,"E4.20.0"),sQuery(id+"F0.wireOp",EDGE,"E4.20.1"),sQuery(id+"F0.wireOp",EDGE,"E4.20.2"),sQuery(id+"F0.wireOp",EDGE,"E4.20.3"),sQuery(id+"F0.wireOp",EDGE,"E4.20.4"),sQuery(id+"F0.wireOp",EDGE,"E4.20.5"),sQuery(id+"F0.wireOp",EDGE,"E4.20.6"),sQuery(id+"F0.wireOp",EDGE,"E4.20.7"),sQuery(id+"F0.wireOp",EDGE,"E4.21.0"),sQuery(id+"F0.wireOp",EDGE,"E4.21.1"),sQuery(id+"F0.wireOp",EDGE,"E4.21.2"),sQuery(id+"F0.wireOp",EDGE,"E4.21.3"),sQuery(id+"F0.wireOp",EDGE,"E4.21.4"),sQuery(id+"F0.wireOp",EDGE,"E4.21.5"),sQuery(id+"F0.wireOp",EDGE,"E4.21.6"),sQuery(id+"F0.wireOp",EDGE,"E4.21.7"),sQuery(id+"F0.wireOp",EDGE,"E4.22.0"),sQuery(id+"F0.wireOp",EDGE,"E4.22.1"),sQuery(id+"F0.wireOp",EDGE,"E4.22.2"),sQuery(id+"F0.wireOp",EDGE,"E4.22.3"),sQuery(id+"F0.wireOp",EDGE,"E4.22.4"),sQuery(id+"F0.wireOp",EDGE,"E4.22.5"),sQuery(id+"F0.wireOp",EDGE,"E4.22.6"),sQuery(id+"F0.wireOp",EDGE,"E4.22.7"),sQuery(id+"F0.wireOp",EDGE,"E4.23.0"),sQuery(id+"F0.wireOp",EDGE,"E4.23.1"),sQuery(id+"F0.wireOp",EDGE,"E4.23.2"),sQuery(id+"F0.wireOp",EDGE,"E4.23.3"),sQuery(id+"F0.wireOp",EDGE,"E4.23.4"),sQuery(id+"F0.wireOp",EDGE,"E4.23.5"),sQuery(id+"F0.wireOp",EDGE,"E4.23.6"),sQuery(id+"F0.wireOp",EDGE,"E4.23.7"),sQuery(id+"F0.wireOp",EDGE,"E4.24.0"),sQuery(id+"F0.wireOp",EDGE,"E4.24.1"),sQuery(id+"F0.wireOp",EDGE,"E4.24.2"),sQuery(id+"F0.wireOp",EDGE,"E4.24.3"),sQuery(id+"F0.wireOp",EDGE,"E4.24.4"),sQuery(id+"F0.wireOp",EDGE,"E4.24.5"),sQuery(id+"F0.wireOp",EDGE,"E4.24.6"),sQuery(id+"F0.wireOp",EDGE,"E4.24.7"),sQuery(id+"F0.wireOp",EDGE,"E4.25.0"),sQuery(id+"F0.wireOp",EDGE,"E4.25.1"),sQuery(id+"F0.wireOp",EDGE,"E4.25.2"),sQuery(id+"F0.wireOp",EDGE,"E4.25.3"),sQuery(id+"F0.wireOp",EDGE,"E4.25.4"),sQuery(id+"F0.wireOp",EDGE,"E4.25.5"),sQuery(id+"F0.wireOp",EDGE,"E4.25.6"),sQuery(id+"F0.wireOp",EDGE,"E4.25.7"),sQuery(id+"F0.wireOp",EDGE,"E5")])],"isStart":true});
            var sketch = newSketch(context, id + "F2", { "sketchPlane" : qUnion([Q0])});
            skCircle(sketch, "E6", {"center": v(0.01, 0) * mm, "radius": 12.5 * mm});
            skCircle(sketch, "E7", {"center": v(0.01, 0) * mm, "radius": 2.7 * mm});
            skSolve(sketch);
        }
        {
            var Q0;
            Q0 = qSketchRegion(id + "F2", true);
            extrude(context, id + "F3", {"entities" : qUnion([Q0]), "operationType" : NewBodyOperationType.ADD, "depth" : 8 * mm});
        }
    });
